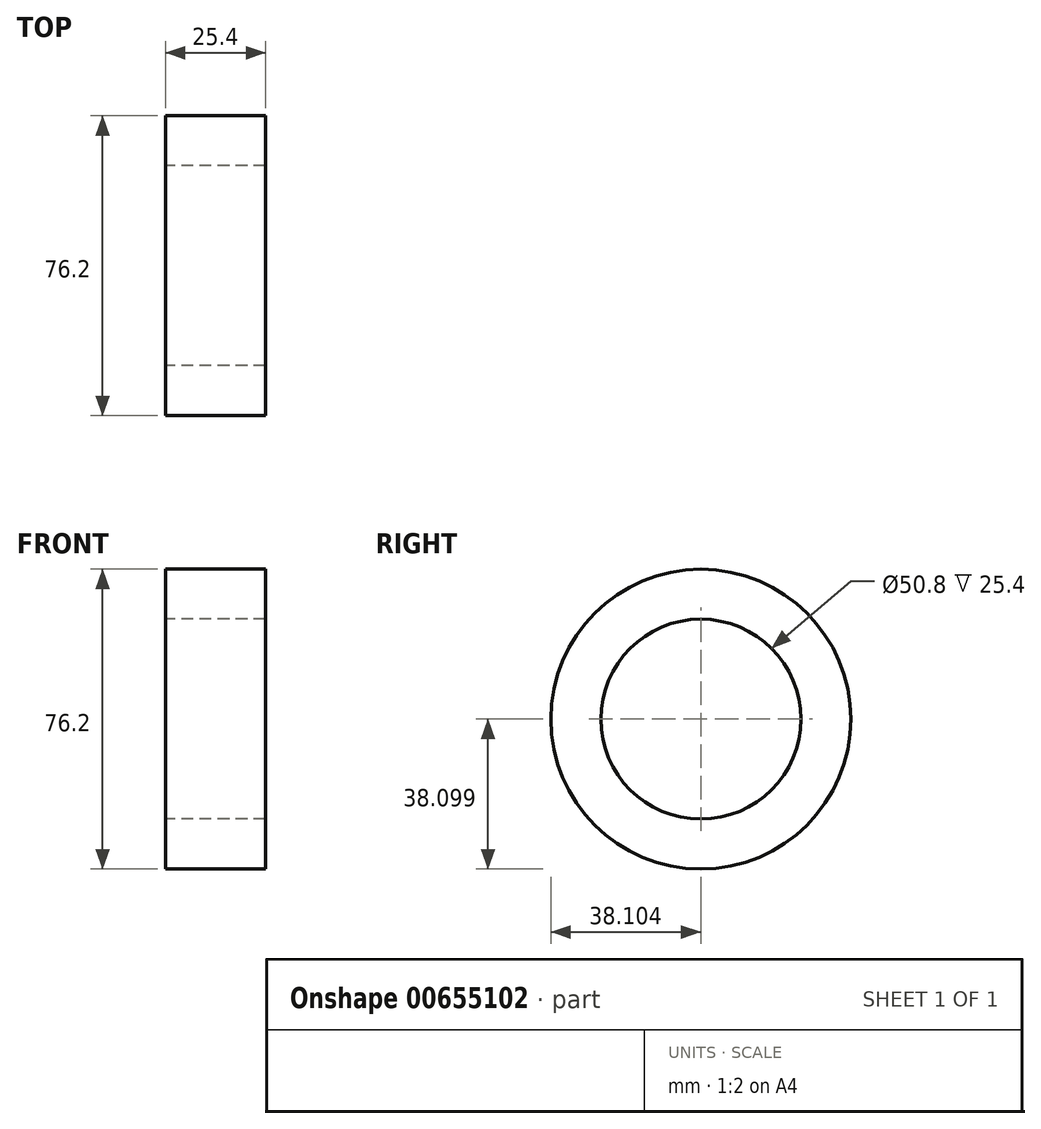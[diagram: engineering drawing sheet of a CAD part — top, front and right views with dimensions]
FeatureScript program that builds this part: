
annotation { "Feature Type Name" : "Feature", "Feature Type Description" : "" }
export const myFeature = defineFeature(function(context is Context, id is Id, definition is map)
    precondition{}
    {
        {
            var Q0;
            Q0=qCreatedBy(makeId("Right.planeOp"),FACE);
            var sketch = newSketch(context, id + "F0", { "sketchPlane" : qUnion([Q0])});
            skCircle(sketch, "E0", {"center": v(-105.62, 36.29) * mm, "radius": 38.1 * mm});
            skCircle(sketch, "E1", {"center": v(-105.62, 36.29) * mm, "radius": 25.4 * mm});
            skCircle(sketch, "E2", {"center": v(-105.62, 36.29) * mm, "radius": 19.05 * mm});
            skCircle(sketch, "E3", {"center": v(-105.62, 36.29) * mm, "radius": 15.88 * mm});
            skCircle(sketch, "E4", {"center": v(-105.62, 36.29) * mm, "radius": 14.29 * mm});
            skSolve(sketch);
        }
        {
            var Q0;
            Q0=makeQuery(id+"F0.imprint","IMPRINT",FACE,{"disambiguationData":[TD([[makeQuery(id+"F0.imprint","IMPRINT",EDGE,{"derivedFrom":sQuery(id+"F0.wireOp",EDGE,"E0")}),1.0]])]});
            extrude(context, id + "F1", {"entities" : qUnion([Q0]), "depth" : 25.4 * mm, "offsetDistance" : 25.4 * mm});
        }
    });
